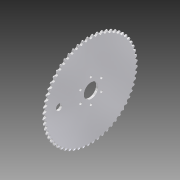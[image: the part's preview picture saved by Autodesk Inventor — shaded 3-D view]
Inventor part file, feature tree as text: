
AUTODESK INVENTOR PART (.ipt)
format: ipt  version: 2013 (Build 170138000, 138)  size: 1,097,216 bytes
history: native  units: mm (DEFAULTED — no unit token found)
features: sketch x5, hole x3, pattern_circular x2, other x1, extrude x1
ambient origin geometry x8: Origin, YZ Plane, XZ Plane, XY Plane, X Axis, Y Axis, Z Axis, Center Point
bodies: Solid1 (feature_tree)
feature tree (12):
  other  "Sprocket Blank"
  extrude  "Tooth Profile"  Depth=93.731413mm
  hole  "Bore"  [1 undecoded]
  pattern_circular  "Circular Pattern2"  [2 undecoded]
  hole  "Hole3"  [1 undecoded]
  pattern_circular  "Circular Pattern3"  [2 undecoded]
  hole  "Hole4"  [1 undecoded]
  sketch  "Sketch1"  dims[d0=4.276725mm d1=93.731413mm]
  sketch  "Sketch2"  dims[d2=4.7625mm d3=10.125075mm]
  sketch  "Sketch5"  dims[d4=90.0deg]
  sketch  "Sketch10"  dims[d9=181.997248mm]
  sketch  "Sketch11"  dims[d10=0.523599mm d11=7.051523mm d12=3.287845mm d13=0.369555mm d14=4.069007mm d15=2.388759mm d16=6.6548mm d17=5.1816mm d18=25.4mm d19=0.0mm d42=28.5623mm d43=12.7mm d44=9.525mm d45=6.35mm d46=14.3117mm d47=19.05mm d48=20.594885mm d53=600.0mm d55=360.0deg d56=23.8125mm d57=5.2324mm d58=12.7mm d59=9.525mm d60=6.35mm d61=14.3117mm d62=19.05mm d63=20.594885mm d64=60.0mm d66=360.0deg d67=63.5mm d68=180.0deg d69=12.7mm d70=19.05mm d71=9.525mm d72=6.35mm d73=14.3117mm d74=25.4mm d75=20.594885mm]
note: 7 required parameter values undecoded (feature->parameter linkage not recoverable at this tier; creation-order binding heuristic only, values carry confidence <= 0.55)
